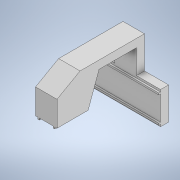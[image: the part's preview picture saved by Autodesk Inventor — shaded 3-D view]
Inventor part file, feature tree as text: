
AUTODESK INVENTOR PART (.ipt)
format: ipt  version: 2020 (Build 240168000, 168)  size: 163,840 bytes
history: native  units: in
note: dims shown in document units (in); Inventor stores cm internally (conversion verified against a paired STEP export)
features: extrude x4, sketch x4
ambient origin geometry x8: Origin, YZ Plane, XZ Plane, XY Plane, X Axis, Y Axis, Z Axis, Center Point
bodies: Solid1 (feature_tree)
feature tree (8):
  extrude  "Extrusion1"  Depth=11.811in
  extrude  "Extrusion2"  Depth=25.5906in TaperAngle=0.0deg
  extrude  "Extrusion3"  Depth=2.9528in
  extrude  "Extrusion4"  Depth=23.622in
  sketch  "Sketch1"  dims[d0=10.1181in d1=11.811in]
  sketch  "Sketch2"  dims[d2=2.9528in d3=25.5906in d4=0.0in]
  sketch  "Sketch3"  dims[d5=7.874in d6=0.0in d7=2.9528in]
  sketch  "Sketch4"  dims[d8=11.811in d9=23.622in d10=11.0236in d11=17.7165in d12=13.7795in d13=7.874in d22=2.3622in d23=0.7874in d24=0.6299in d25=0.6299in d26=0.0in d27=0.0in d28=0.7874in d29=0.6299in d30=0.6299in d31=0.0in d32=0.0in]
